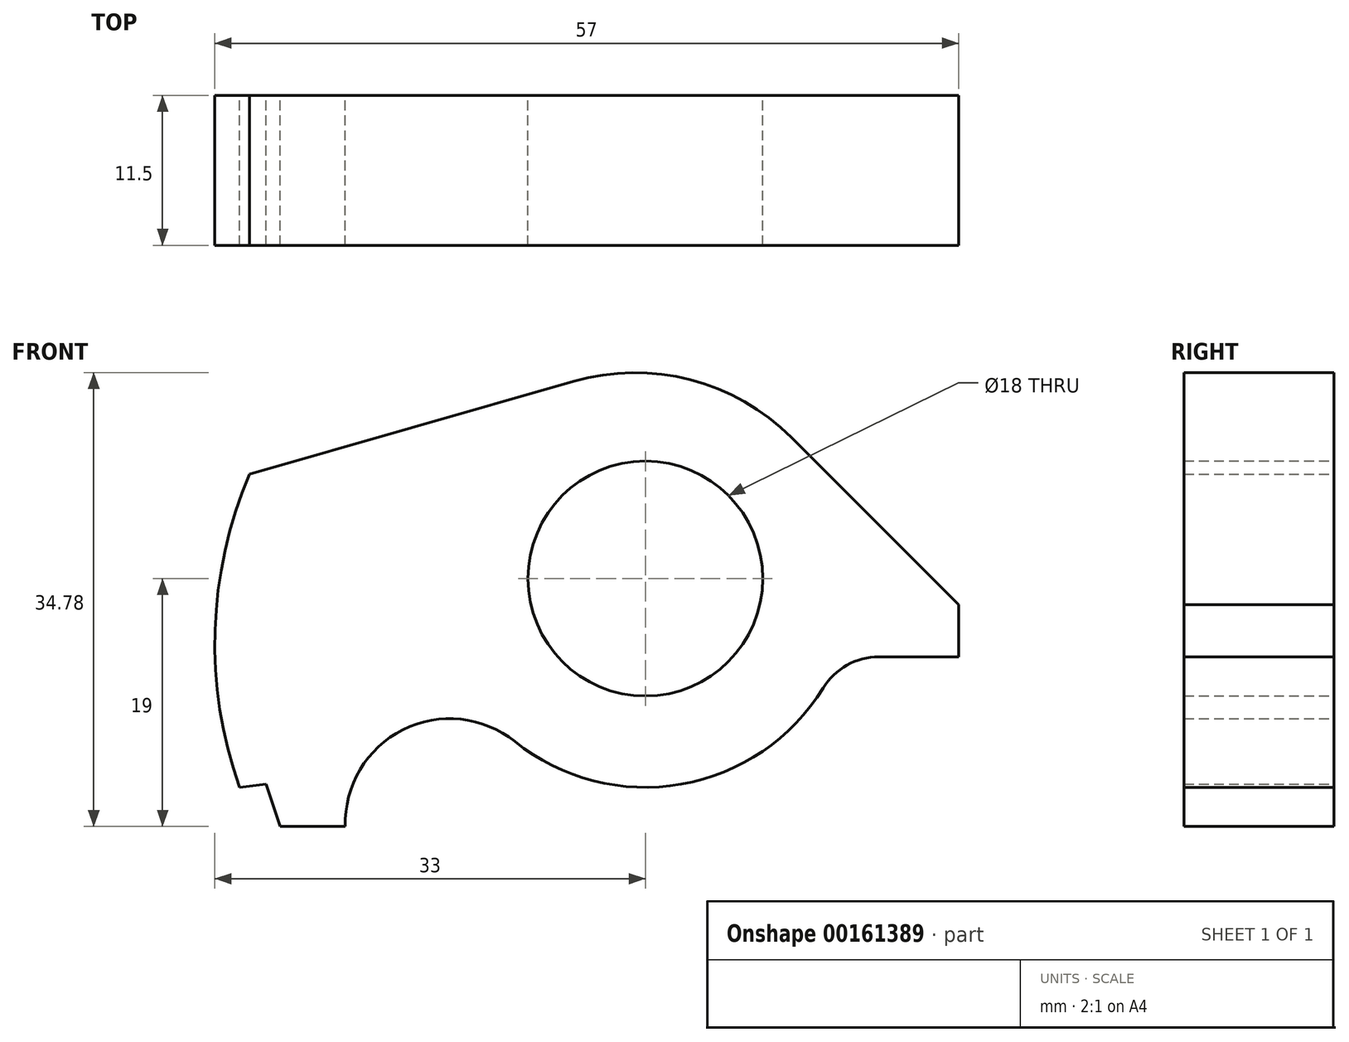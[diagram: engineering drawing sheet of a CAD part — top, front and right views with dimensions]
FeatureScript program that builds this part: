
annotation { "Feature Type Name" : "Feature", "Feature Type Description" : "" }
export const myFeature = defineFeature(function(context is Context, id is Id, definition is map)
    precondition{}
    {
        {
            var Q0;
            Q0=qCreatedBy(makeId("Front.planeOp"),FACE);
            var sketch = newSketch(context, id + "F0", { "sketchPlane" : qUnion([Q0])});
            skCircle(sketch, "E0", {"center": v(0, 0) * mm, "radius": 9 * mm});
            skPoint(sketch, "E1", {"position": v(0, -5) * mm});
            skLineSegment(sketch, "E2", {"start": v(-36.05, 0) * mm, "end": v(42.13, 0) * mm, "construction": true});
            skLineSegment(sketch, "E3", {"start": v(24, -2) * mm, "end": v(24, -6) * mm});
            skLineSegment(sketch, "E4", {"start": v(24, -2) * mm, "end": v(11.2, 10.8) * mm});
            skArc(sketch, "E5", {"start": v(-10, -12.49) * mm, "mid": v(2.74, -15.76) * mm, "end": v(13.63, -8.38) * mm});
            skLineSegment(sketch, "E6", {"start": v(-31.11, -16) * mm, "end": v(-29.09, -15.75) * mm});
            skLineSegment(sketch, "E7", {"start": v(-29.09, -15.75) * mm, "end": v(-28, -19) * mm});
            skLineSegment(sketch, "E8", {"start": v(24, -6) * mm, "end": v(17.89, -6) * mm});
            skArc(sketch, "E9", {"start": v(13.63, -8.38) * mm, "mid": v(15.45, -6.64) * mm, "end": v(17.89, -6) * mm});
            skPoint(sketch, "E10", {"position": v(-15, -18.73) * mm});
            skArc(sketch, "E11", {"start": v(-30.33, 8) * mm, "mid": v(-32.98, -3.93) * mm, "end": v(-31.11, -16) * mm});
            skPoint(sketch, "E12.orphan", {"position": v(-32.54, 7.48) * mm});
            skPoint(sketch, "E13.orphan", {"position": v(-33.81, -16.33) * mm});
            skArc(sketch, "E14", {"start": v(-10, -12.49) * mm, "mid": v(-18.58, -11.58) * mm, "end": v(-23, -19) * mm});
            skLineSegment(sketch, "E15", {"start": v(-28, -19) * mm, "end": v(-23, -19) * mm});
            skPoint(sketch, "E16.orphan", {"position": v(-12.05, 11.99) * mm});
            skLineSegment(sketch, "E17", {"start": v(-30.33, 8) * mm, "end": v(-5.5, 15.12) * mm});
            skArc(sketch, "E18", {"start": v(-5.5, 15.12) * mm, "mid": v(3.44, 15.24) * mm, "end": v(11.2, 10.8) * mm});
            skSolve(sketch);
        }
        {
            var Q0;
            Q0 = qSketchRegion(id + "F0", true);
            extrude(context, id + "F1", {"entities" : qUnion([Q0]), "depth" : 11.5 * mm});
        }
    });
